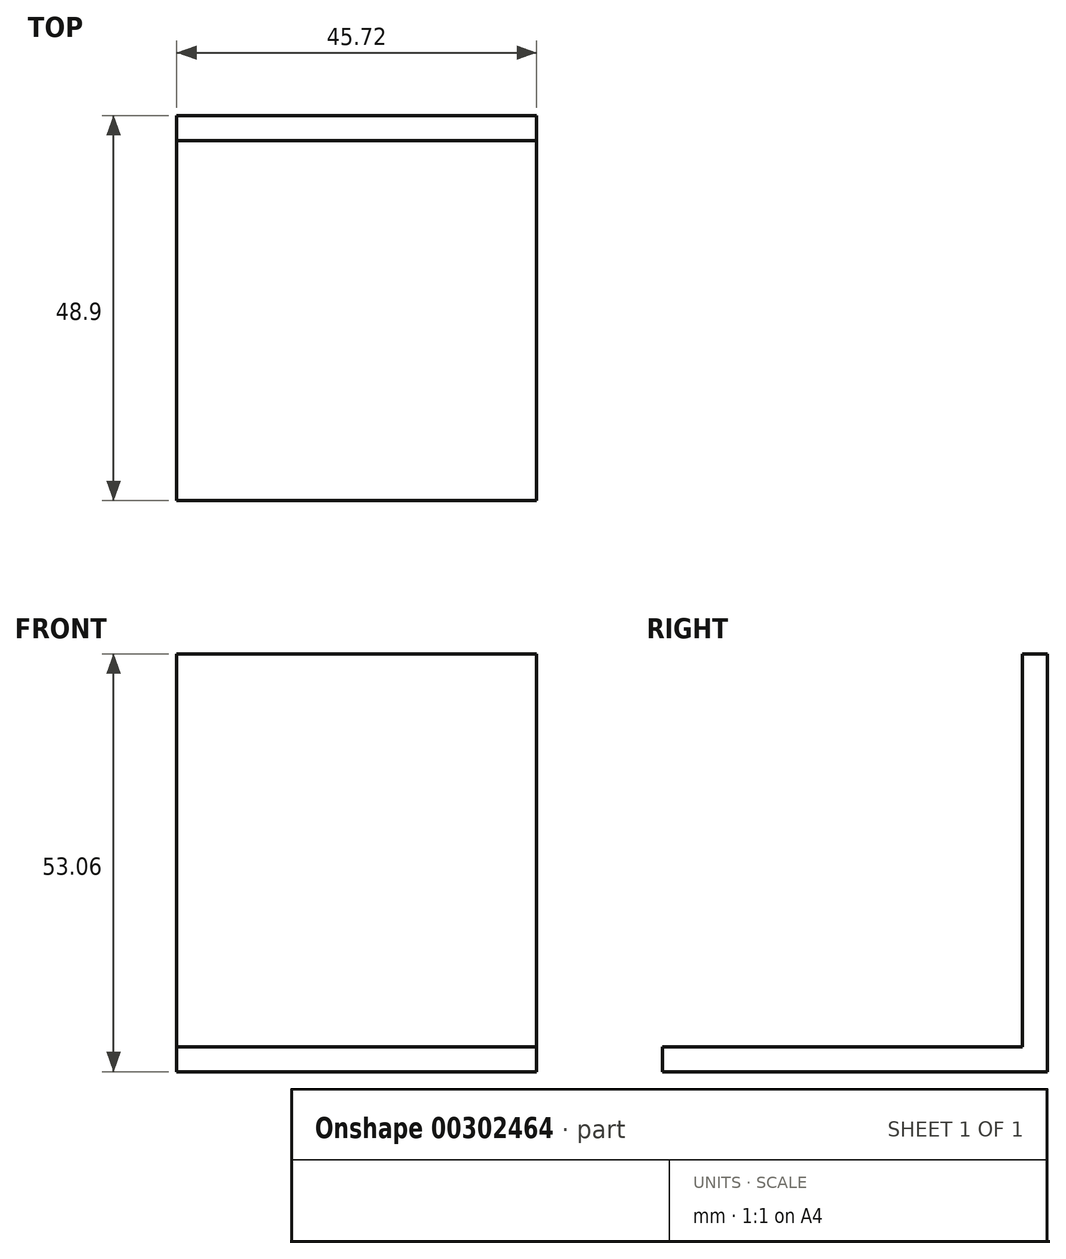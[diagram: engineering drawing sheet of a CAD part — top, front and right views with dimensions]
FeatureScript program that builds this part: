
annotation { "Feature Type Name" : "Feature", "Feature Type Description" : "" }
export const myFeature = defineFeature(function(context is Context, id is Id, definition is map)
    precondition{}
    {
        {
            var Q0;
            Q0=qCreatedBy(makeId("Front.planeOp"),FACE);
            var sketch = newSketch(context, id + "F0", { "sketchPlane" : qUnion([Q0])});
            skLineSegment(sketch, "E0.bottom", {"start": v(-37.77, 76.2) * mm, "end": v(7.95, 76.2) * mm});
            skLineSegment(sketch, "E0.top", {"start": v(-37.77, 0) * mm, "end": v(7.95, 0) * mm});
            skLineSegment(sketch, "E0.left", {"start": v(-37.77, 76.2) * mm, "end": v(-37.77, 0) * mm});
            skLineSegment(sketch, "E0.right", {"start": v(7.95, 76.2) * mm, "end": v(7.95, 0) * mm});
            skSolve(sketch);
        }
        {
            var Q0;
            Q0 = qSketchRegion(id + "F0", true);
            extrude(context, id + "F1", {"entities" : qUnion([Q0]), "depth" : 3.17 * mm});
        }
        {
            var Q0;
            Q0=makeQuery(id+"F1.opExtrude","CAP_FACE",FACE,{"disambiguationData":[OSD([sQuery(id+"F0.wireOp",EDGE,"E0.bottom"),sQuery(id+"F0.wireOp",EDGE,"E0.top"),sQuery(id+"F0.wireOp",EDGE,"E0.left"),sQuery(id+"F0.wireOp",EDGE,"E0.right")])],"isStart":false});
            var sketch = newSketch(context, id + "F2", { "sketchPlane" : qUnion([Q0])});
            skLineSegment(sketch, "E1.bottom", {"start": v(-37.77, 3.18) * mm, "end": v(7.95, 3.18) * mm});
            skLineSegment(sketch, "E1.top", {"start": v(-37.77, 0) * mm, "end": v(7.95, 0) * mm});
            skLineSegment(sketch, "E1.left", {"start": v(-37.77, 3.18) * mm, "end": v(-37.77, 0) * mm});
            skLineSegment(sketch, "E1.right", {"start": v(7.95, 3.18) * mm, "end": v(7.95, 0) * mm});
            skSolve(sketch);
        }
        {
            var Q0;
            Q0 = qSketchRegion(id + "F2", true);
            extrude(context, id + "F3", {"entities" : qUnion([Q0]), "operationType" : NewBodyOperationType.ADD, "depth" : 45.72 * mm});
        }
        {
            var Q0;
            Q0=makeQuery(id+"F1.opExtrude","CAP_FACE",FACE,{"disambiguationData":[OSD([sQuery(id+"F0.wireOp",EDGE,"E0.bottom"),sQuery(id+"F0.wireOp",EDGE,"E0.top"),sQuery(id+"F0.wireOp",EDGE,"E0.left"),sQuery(id+"F0.wireOp",EDGE,"E0.right")])],"isStart":false});
            var sketch = newSketch(context, id + "F4", { "sketchPlane" : qUnion([Q0])});
            skLineSegment(sketch, "E2.bottom", {"start": v(-37.77, 64.4) * mm, "end": v(7.95, 64.4) * mm});
            skLineSegment(sketch, "E2.top", {"start": v(-37.77, 76.2) * mm, "end": v(7.95, 76.2) * mm});
            skLineSegment(sketch, "E2.left", {"start": v(-37.77, 64.4) * mm, "end": v(-37.77, 76.2) * mm});
            skLineSegment(sketch, "E2.right", {"start": v(7.95, 64.4) * mm, "end": v(7.95, 76.2) * mm});
            skLineSegment(sketch, "E3.bottom", {"start": v(-37.77, 53.06) * mm, "end": v(7.95, 53.06) * mm});
            skLineSegment(sketch, "E3.left", {"start": v(-37.77, 53.06) * mm, "end": v(-37.77, 64.4) * mm});
            skLineSegment(sketch, "E3.right", {"start": v(7.95, 53.06) * mm, "end": v(7.95, 64.4) * mm});
            skSolve(sketch);
        }
        {
            var Q0;
            Q0 = qSketchRegion(id + "F4", true);
            extrude(context, id + "F5", {"entities" : qUnion([Q0]), "operationType" : NewBodyOperationType.REMOVE, "oppositeDirection" : true, "depth" : 25.4 * mm});
        }
    });
